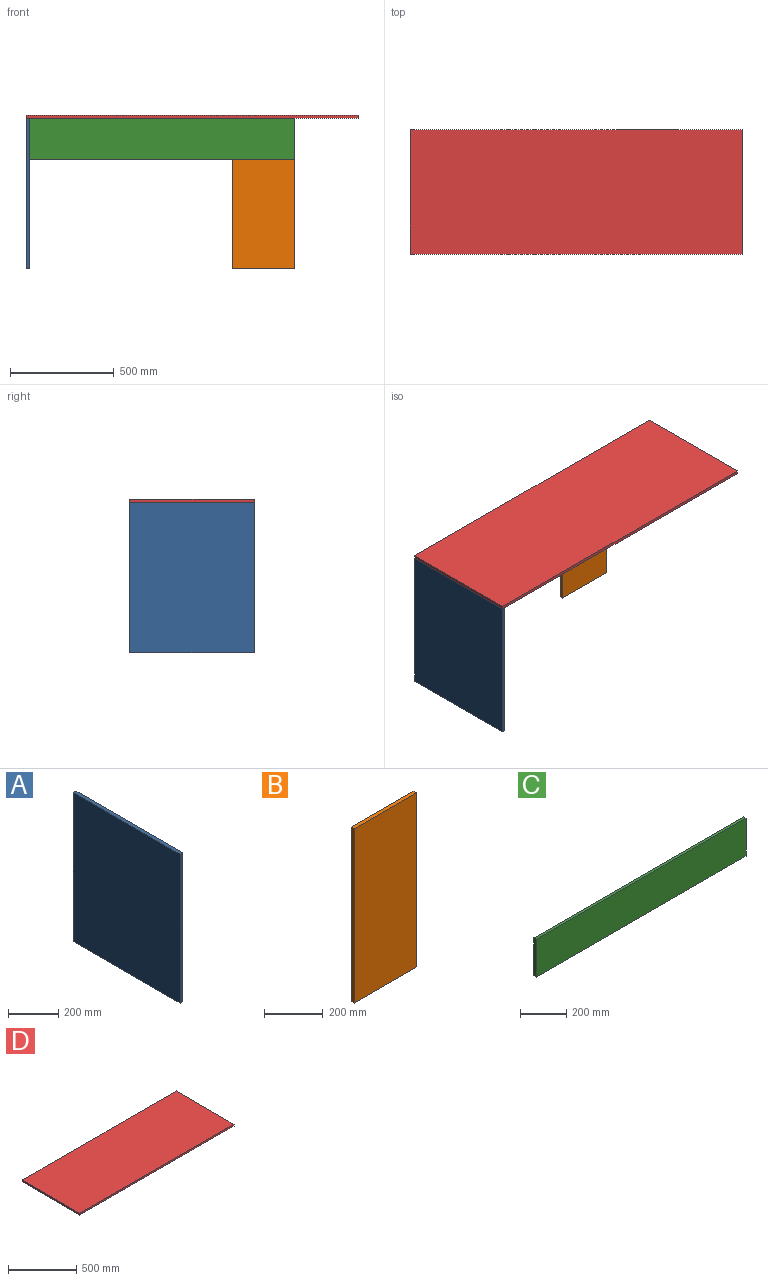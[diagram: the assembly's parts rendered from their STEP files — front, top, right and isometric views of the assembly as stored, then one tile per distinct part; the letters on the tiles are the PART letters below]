
ASSEMBLY  parts=4 mates=3
PART A: 6 faces, bbox 15x600x725 mm
  f0: plane 600x15mm, normal (0,0,1), area 9000mm2, adj f1,f3,f4,f5
  f1: plane 725x15mm, normal (0,-1,0), area 10875mm2, adj f0,f2,f4,f5
  f2: plane 600x15mm, normal (0,0,-1), area 9000mm2, adj f1,f3,f4,f5
  f3: plane 725x15mm, normal (0,1,0), area 10875mm2, adj f0,f2,f4,f5
  f4: plane 725x600mm, normal (1,0,0), area 435000mm2, adj f0,f1,f2,f3
  f5: plane 725x600mm, normal (-1,0,0), area 435000mm2, adj f0,f1,f2,f3
PART B: 6 faces, bbox 300x15x725 mm
  f0: plane 300x15mm, normal (0,0,1), area 4500mm2, adj f1,f3,f4,f5
  f1: plane 725x15mm, normal (-1,0,0), area 10875mm2, adj f0,f2,f4,f5
  f2: plane 300x15mm, normal (0,0,-1), area 4500mm2, adj f1,f3,f4,f5
  f3: plane 725x15mm, normal (1,0,0), area 10875mm2, adj f0,f2,f4,f5
  f4: plane 725x300mm, normal (0,-1,0), area 217500mm2, adj f0,f1,f2,f3
  f5: plane 725x300mm, normal (0,1,0), area 217500mm2, adj f0,f1,f2,f3
PART C: 6 faces, bbox 1280x15x200 mm
  f0: plane 1280x15mm, normal (0,0,1), area 19200mm2, adj f1,f3,f4,f5
  f1: plane 200x15mm, normal (-1,0,0), area 3000mm2, adj f0,f2,f4,f5
  f2: plane 1280x15mm, normal (0,0,-1), area 19200mm2, adj f1,f3,f4,f5
  f3: plane 200x15mm, normal (1,0,0), area 3000mm2, adj f0,f2,f4,f5
  f4: plane 1280x200mm, normal (0,-1,0), area 256000mm2, adj f0,f1,f2,f3
  f5: plane 1280x200mm, normal (0,1,0), area 256000mm2, adj f0,f1,f2,f3
PART D: 6 faces, bbox 1600x600x15 mm
  f0: plane 1600x15mm, normal (0,1,0), area 24000mm2, adj f1,f3,f4,f5
  f1: plane 600x15mm, normal (-1,0,0), area 9000mm2, adj f0,f2,f4,f5
  f2: plane 1600x15mm, normal (0,-1,0), area 24000mm2, adj f1,f3,f4,f5
  f3: plane 600x15mm, normal (1,0,0), area 9000mm2, adj f0,f2,f4,f5
  f4: plane 1600x600mm, normal (0,0,1), area 960000mm2, adj f0,f1,f2,f3
  f5: plane 1600x600mm, normal (0,0,-1), area 960000mm2, adj f0,f1,f2,f3
PLACE A t=(-1079.1,-149.35,-259.61)mm
PLACE B t=(184.08,152.84,-665.9)mm
PLACE C t=(398.69,137.84,-198.38)mm
PLACE D t=(-326.81,-36.35,13.47)mm
MATE fastened C.f3 <-> B.f3  axis (1,0,0) through (215.9,137.84,13.47)mm
MATE fastened A.f1 <-> D.f2  axis (0,1,0) through (-1079.1,-447.16,13.47)mm
MATE fastened B.f5 <-> D.f0  axis (0,1,0) through (215.9,152.84,13.47)mm
